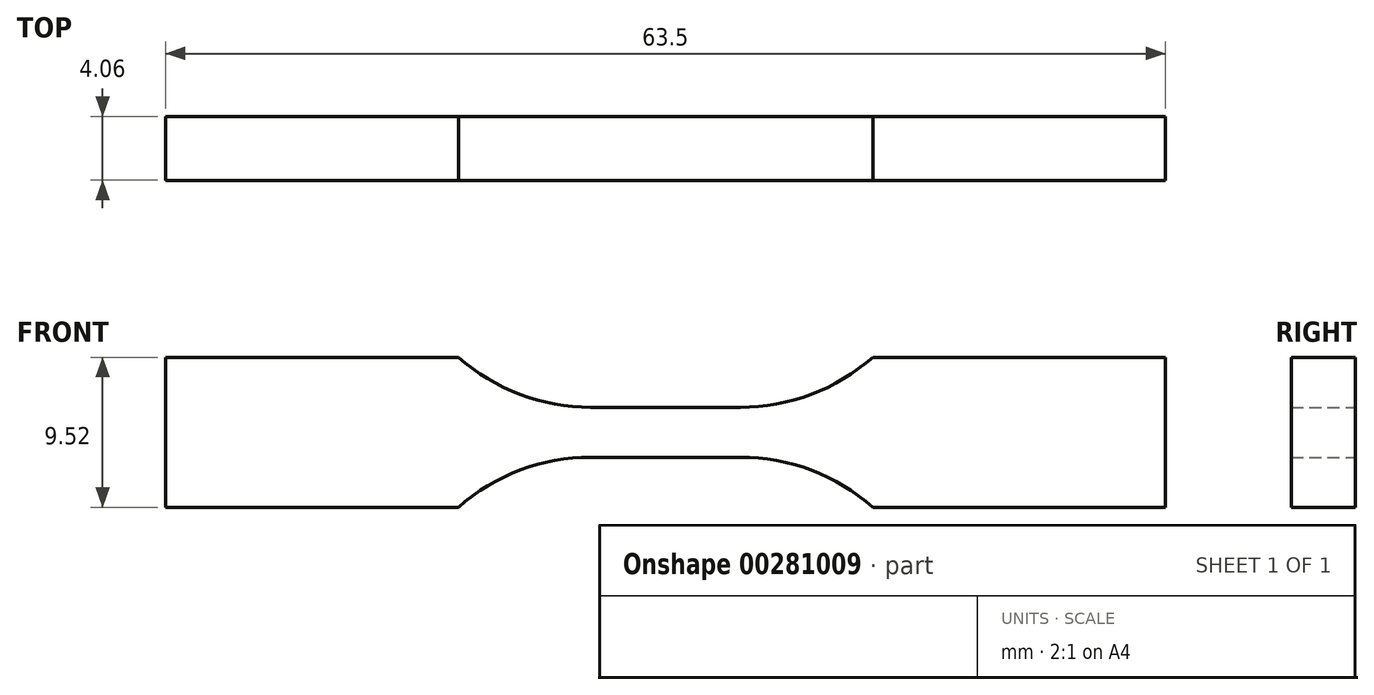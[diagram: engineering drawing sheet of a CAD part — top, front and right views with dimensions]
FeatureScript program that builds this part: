
annotation { "Feature Type Name" : "Feature", "Feature Type Description" : "" }
export const myFeature = defineFeature(function(context is Context, id is Id, definition is map)
    precondition{}
    {
        {
            var Q0;
            Q0=qCreatedBy(makeId("Front.planeOp"),FACE);
            var sketch = newSketch(context, id + "F0", { "sketchPlane" : qUnion([Q0])});
            skLineSegment(sketch, "E0", {"start": v(0, 1.59) * mm, "end": v(4.76, 1.59) * mm});
            skArc(sketch, "E1", {"start": v(4.76, 1.59) * mm, "mid": v(9.25, 2.4) * mm, "end": v(13.16, 4.76) * mm});
            skLineSegment(sketch, "E2", {"start": v(13.16, 4.76) * mm, "end": v(31.75, 4.76) * mm});
            skLineSegment(sketch, "E3", {"start": v(31.75, 4.76) * mm, "end": v(31.75, 0) * mm});
            skLineSegment(sketch, "E4.MirrorCS", {"start": v(0, -1.59) * mm, "end": v(4.76, -1.59) * mm});
            skLineSegment(sketch, "E5.MirrorCS", {"start": v(31.75, -4.76) * mm, "end": v(31.75, 0) * mm});
            skLineSegment(sketch, "E6.MirrorCS", {"start": v(13.16, -4.76) * mm, "end": v(31.75, -4.76) * mm});
            skArc(sketch, "E7.MirrorCS", {"start": v(4.76, -1.59) * mm, "mid": v(9.25, -2.4) * mm, "end": v(13.16, -4.76) * mm});
            skArc(sketch, "E8.MirrorCS", {"start": v(-4.76, -1.59) * mm, "mid": v(-9.25, -2.4) * mm, "end": v(-13.16, -4.76) * mm});
            skLineSegment(sketch, "E9.MirrorCS", {"start": v(-13.16, -4.76) * mm, "end": v(-31.75, -4.76) * mm});
            skArc(sketch, "E10.MirrorCS", {"start": v(-4.76, 1.59) * mm, "mid": v(-9.25, 2.4) * mm, "end": v(-13.16, 4.76) * mm});
            skLineSegment(sketch, "E11.MirrorCS", {"start": v(-13.16, 4.76) * mm, "end": v(-31.75, 4.76) * mm});
            skLineSegment(sketch, "E12.MirrorCS", {"start": v(-31.75, -4.76) * mm, "end": v(-31.75, 0) * mm});
            skLineSegment(sketch, "E13.MirrorCS", {"start": v(0, -1.59) * mm, "end": v(-4.76, -1.59) * mm});
            skLineSegment(sketch, "E14.MirrorCS", {"start": v(-31.75, 4.76) * mm, "end": v(-31.75, 0) * mm});
            skLineSegment(sketch, "E15.MirrorCS", {"start": v(0, 1.59) * mm, "end": v(-4.76, 1.59) * mm});
            skSolve(sketch);
        }
        {
            var Q0;
            Q0 = qSketchRegion(id + "F0", true);
            extrude(context, id + "F1", {"entities" : qUnion([Q0]), "depth" : 4.06 * mm});
        }
    });
